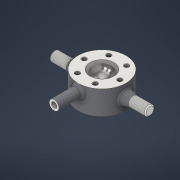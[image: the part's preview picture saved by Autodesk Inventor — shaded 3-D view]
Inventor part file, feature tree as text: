
AUTODESK INVENTOR PART (.ipt)
format: ipt  version: 2022 (Build 260153000, 153)  size: 263,680 bytes
history: native  units: mm
features: sketch x7, extrude x3, chamfer x3, other x2, revolve x2, hole x2, thread x1, mirror x1, pattern_circular x1
ambient origin geometry x8: Origin, YZ Plane, XZ Plane, XY Plane, X Axis, Y Axis, Z Axis, Center Point
bodies: Body1 (feature_tree)
feature tree (22):
  extrude  "Выдавливание4"  Depth=100.0mm
  other  "РабПлоскость10"
  revolve  "Вращение3"
  thread  "Резьба2"
  chamfer  "Фаска2"  Distance=50.0mm
  chamfer  "Фаска3"  Distance=100.0mm
  mirror  "Зеркальное отражение2"
  revolve  "Вращение4"
  hole  "Отверстие4"  [1 undecoded]
  pattern_circular  "Круговой массив2"  [2 undecoded]
  other  "РабПлоскость12"
  extrude  "Выдавливание9"  TaperAngle=15.0deg  [1 undecoded]
  chamfer  "Фаска4"  Angle=90.0deg  [1 undecoded]
  hole  "Отверстие5"  [1 undecoded]
  extrude  "Выдавливание10"  Depth=2.0mm TaperAngle=45.0deg
  sketch  "Эскиз18"
  sketch  "Эскиз19"
  sketch  "Эскиз22"
  sketch  "Эскиз23"
  sketch  "Эскиз28"
  sketch  "Эскиз29"
  sketch  "Эскиз30"
note: 6 required parameter values undecoded (feature->parameter linkage not recoverable at this tier; creation-order binding heuristic only, values carry confidence <= 0.55)
